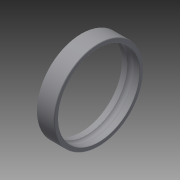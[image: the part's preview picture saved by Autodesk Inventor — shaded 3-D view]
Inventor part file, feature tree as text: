
AUTODESK INVENTOR PART (.ipt)
format: ipt  version: 2014 SP2 (Build 180246200, 246)  size: 150,528 bytes
history: native  units: mm
features: other x7, revolve x1, sketch x1
ambient origin geometry x8: Origin, YZ Plane, XZ Plane, XY Plane, X Axis, Y Axis, Z Axis, Center Point
bodies: Solid1 (feature_tree)
feature tree (9):
  revolve  "Revolution1"  [1 undecoded]
  other  "1_XY"
  other  "1_YZ"
  other  "1_ZX"
  other  "1_X"
  other  "1_Y"
  other  "1_Z"
  other  "1_Center"
  sketch  "Sketch_1"  dims[d0=360.0deg]
note: 1 required parameter value undecoded (feature->parameter linkage not recoverable at this tier; creation-order binding heuristic only, values carry confidence <= 0.55)
